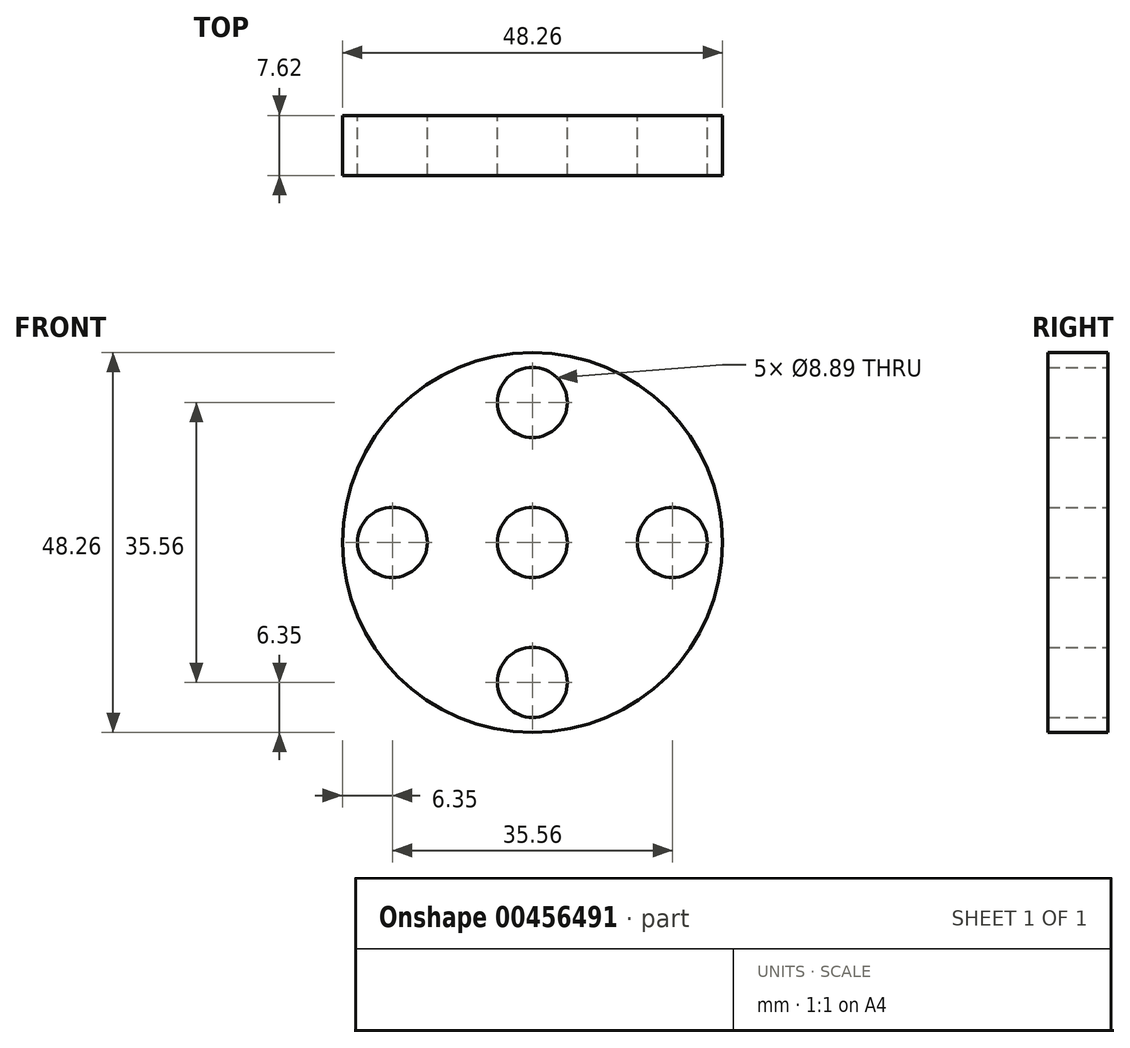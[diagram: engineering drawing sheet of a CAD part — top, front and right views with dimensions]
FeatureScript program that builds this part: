
annotation { "Feature Type Name" : "Feature", "Feature Type Description" : "" }
export const myFeature = defineFeature(function(context is Context, id is Id, definition is map)
    precondition{}
    {
        {
            var Q0;
            Q0=qCreatedBy(makeId("Front.planeOp"),FACE);
            var sketch = newSketch(context, id + "F0", { "sketchPlane" : qUnion([Q0])});
            skCircle(sketch, "E0", {"center": v(0, 0) * mm, "radius": 4.45 * mm});
            skCircle(sketch, "E1", {"center": v(0, 0) * mm, "radius": 6.35 * mm});
            skCircle(sketch, "E2", {"center": v(0, 17.78) * mm, "radius": 4.45 * mm});
            skCircle(sketch, "E3", {"center": v(0, 17.78) * mm, "radius": 6.35 * mm});
            skCircle(sketch, "E4", {"center": v(0, -17.78) * mm, "radius": 4.45 * mm});
            skCircle(sketch, "E5", {"center": v(0, -17.78) * mm, "radius": 6.35 * mm});
            skCircle(sketch, "E6", {"center": v(17.78, 0) * mm, "radius": 4.45 * mm});
            skCircle(sketch, "E7", {"center": v(17.78, 0) * mm, "radius": 6.35 * mm});
            skCircle(sketch, "E8", {"center": v(-17.78, 0) * mm, "radius": 4.45 * mm});
            skCircle(sketch, "E9", {"center": v(-17.78, 0) * mm, "radius": 6.35 * mm});
            skLineSegment(sketch, "E10", {"start": v(-6.35, 17.78) * mm, "end": v(-6.35, 0) * mm});
            skLineSegment(sketch, "E11", {"start": v(6.35, 17.78) * mm, "end": v(6.35, 0) * mm});
            skLineSegment(sketch, "E12", {"start": v(17.78, 6.35) * mm, "end": v(0, 6.35) * mm});
            skLineSegment(sketch, "E13", {"start": v(17.78, -6.35) * mm, "end": v(0, -6.35) * mm});
            skLineSegment(sketch, "E14", {"start": v(-6.35, -17.78) * mm, "end": v(-6.35, 0) * mm});
            skLineSegment(sketch, "E15", {"start": v(6.35, -17.78) * mm, "end": v(6.35, 0) * mm});
            skLineSegment(sketch, "E16", {"start": v(-17.78, 6.35) * mm, "end": v(0, 6.35) * mm});
            skLineSegment(sketch, "E17", {"start": v(-17.78, -6.35) * mm, "end": v(0, -6.35) * mm});
            skCircle(sketch, "E18", {"center": v(0, 0) * mm, "radius": 24.13 * mm});
            skSolve(sketch);
        }
        {
            var Q0;
            Q0=qSketchRegion(id+"F0",true);
            var Q1;
            Q1=makeQuery(id+"F0.imprint","IMPRINT",FACE,{"disambiguationData":[TD([[makeQuery(id+"F0.imprint","IMPRINT",EDGE,{"derivedFrom":sQuery(id+"F0.wireOp",EDGE,"E0")}),-1.0]])]});
            var Q2;
            {var subQ0=sQuery(id+"F0.wireOp",EDGE,"Kdj68EMA-EZRf-t48A-a07Z-1QglQ40iLiN1");Q2=makeQuery(id+"F0.imprint","IMPRINT",FACE,{"disambiguationData":[TD([[makeQuery(id+"F0.imprint","IMPRINT",EDGE,{"derivedFrom":subQ0}),1.0]])]});}
            var Q3;
            {var subQ0=sQuery(id+"F0.wireOp",EDGE,"IB2gJiYN-Zbc6-PHf5-ZDkJ-AlS4u5yRiTVI");Q3=makeQuery(id+"F0.imprint","IMPRINT",FACE,{"disambiguationData":[TD([[makeQuery(id+"F0.imprint","IMPRINT",EDGE,{"derivedFrom":subQ0}),1.0]])]});}
            var Q4;
            {var subQ0=sQuery(id+"F0.wireOp",EDGE,"0Rht0vSG-rdW4-fYld-ASEw-sdk48khHN10M");Q4=makeQuery(id+"F0.imprint","IMPRINT",FACE,{"disambiguationData":[TD([[makeQuery(id+"F0.imprint","IMPRINT",EDGE,{"derivedFrom":subQ0}),-1.0]])]});}
            var Q5;
            {var subQ0=sQuery(id+"F0.wireOp",EDGE,"7g5qWJER-UkHk-XB4v-vlxq-Ywh3V0gzCt1J");Q5=makeQuery(id+"F0.imprint","IMPRINT",FACE,{"disambiguationData":[TD([[makeQuery(id+"F0.imprint","IMPRINT",EDGE,{"derivedFrom":subQ0}),-1.0]])]});}
            var Q6;
            {var subQ0=sQuery(id+"F0.wireOp",EDGE,"yTIMhHz3-IvRj-t1zn-yk0A-B27OQOZ1rXdA");Q6=makeQuery(id+"F0.imprint","IMPRINT",FACE,{"disambiguationData":[TD([[makeQuery(id+"F0.imprint","IMPRINT",EDGE,{"derivedFrom":subQ0}),1.0]])]});}
            var Q7;
            {var subQ0=sQuery(id+"F0.wireOp",EDGE,"zt7eYoZQ-1qTK-d0Ye-JGOG-YsbcoZRo1iPv");Q7=makeQuery(id+"F0.imprint","IMPRINT",FACE,{"disambiguationData":[TD([[makeQuery(id+"F0.imprint","IMPRINT",EDGE,{"derivedFrom":subQ0}),1.0]])]});}
            var Q8;
            {var subQ0=sQuery(id+"F0.wireOp",EDGE,"4NbvyGo8-oQjs-yzer-XTdA-Bz790yNYk6cl");Q8=makeQuery(id+"F0.imprint","IMPRINT",FACE,{"disambiguationData":[TD([[makeQuery(id+"F0.imprint","IMPRINT",EDGE,{"derivedFrom":subQ0}),-1.0]])]});}
            var Q9;
            {var subQ0=sQuery(id+"F0.wireOp",EDGE,"eqKnKHy1-V1mz-GWpX-vf4M-KMWb575NkPCI");Q9=makeQuery(id+"F0.imprint","IMPRINT",FACE,{"disambiguationData":[TD([[makeQuery(id+"F0.imprint","IMPRINT",EDGE,{"derivedFrom":subQ0}),-1.0]])]});}
            var Q10;
            {var subQ0=sQuery(id+"F0.wireOp",EDGE,"4dZgK9fm-a6ys-O8Km-lK4I-ZBlqT9DDIq2p");Q10=makeQuery(id+"F0.imprint","IMPRINT",FACE,{"disambiguationData":[TD([[makeQuery(id+"F0.imprint","IMPRINT",EDGE,{"derivedFrom":subQ0}),1.0]])]});}
            var Q11;
            {var subQ0=sQuery(id+"F0.wireOp",EDGE,"eZOobQb2-sPjm-IE9f-PYXj-G9QqCMmR5pJa");Q11=makeQuery(id+"F0.imprint","IMPRINT",FACE,{"disambiguationData":[TD([[makeQuery(id+"F0.imprint","IMPRINT",EDGE,{"derivedFrom":subQ0}),1.0]])]});}
            var Q12;
            {var subQ0=sQuery(id+"F0.wireOp",EDGE,"Rj4KL7sm-qs8i-fHab-Xu34-aNx6nAbFgW3L");Q12=makeQuery(id+"F0.imprint","IMPRINT",FACE,{"disambiguationData":[TD([[makeQuery(id+"F0.imprint","IMPRINT",EDGE,{"derivedFrom":subQ0}),-1.0]])]});}
            var Q13;
            {var subQ0=sQuery(id+"F0.wireOp",EDGE,"GUNANnpx-HFxo-DPJl-9vIq-FGsHx3uaFTqo");Q13=makeQuery(id+"F0.imprint","IMPRINT",FACE,{"disambiguationData":[TD([[makeQuery(id+"F0.imprint","IMPRINT",EDGE,{"derivedFrom":subQ0}),-1.0]])]});}
            var Q14;
            {var subQ0=sQuery(id+"F0.wireOp",EDGE,"IDcZSpyX-G8bH-AgFG-lNg4-9X1LZLpxGCfa");Q14=makeQuery(id+"F0.imprint","IMPRINT",FACE,{"disambiguationData":[TD([[makeQuery(id+"F0.imprint","IMPRINT",EDGE,{"derivedFrom":subQ0}),-1.0]])]});}
            var Q15;
            {var subQ0=sQuery(id+"F0.wireOp",EDGE,"RcCAguLE-jov0-NsOQ-J9fd-5aWVPCAP70dy");Q15=makeQuery(id+"F0.imprint","IMPRINT",FACE,{"disambiguationData":[TD([[makeQuery(id+"F0.imprint","IMPRINT",EDGE,{"derivedFrom":subQ0}),1.0]])]});}
            var Q16;
            {var subQ0=sQuery(id+"F0.wireOp",EDGE,"3mko06cv-CCnZ-XxRW-BRVZ-f3iim2jyQPBJ");Q16=makeQuery(id+"F0.imprint","IMPRINT",FACE,{"disambiguationData":[TD([[makeQuery(id+"F0.imprint","IMPRINT",EDGE,{"derivedFrom":subQ0}),1.0]])]});}
            var Q17;
            {var subQ0=sQuery(id+"F0.wireOp",EDGE,"ipUqtzeX-P4ue-mGOc-rtnN-ZdVFXNdYJOps");Q17=makeQuery(id+"F0.imprint","IMPRINT",FACE,{"disambiguationData":[TD([[makeQuery(id+"F0.imprint","IMPRINT",EDGE,{"derivedFrom":subQ0}),-1.0]])]});}
            var Q18;
            {var subQ0=sQuery(id+"F0.wireOp",EDGE,"ig39oKl3-C4g6-UK27-omIZ-Wn6p40oPa8TG");Q18=makeQuery(id+"F0.imprint","IMPRINT",FACE,{"disambiguationData":[TD([[makeQuery(id+"F0.imprint","IMPRINT",EDGE,{"derivedFrom":subQ0}),1.0]])]});}
            var Q19;
            {var subQ0=sQuery(id+"F0.wireOp",EDGE,"yZy14Uba-DGiZ-CVV4-Hzny-6y7y5RzOsm5Q");Q19=makeQuery(id+"F0.imprint","IMPRINT",FACE,{"disambiguationData":[TD([[makeQuery(id+"F0.imprint","IMPRINT",EDGE,{"derivedFrom":subQ0}),1.0]])]});}
            var Q20;
            {var subQ0=sQuery(id+"F0.wireOp",EDGE,"VIuSlq0m-v5Ym-oCGE-2FKm-41l9RQB9eqMF");Q20=makeQuery(id+"F0.imprint","IMPRINT",FACE,{"disambiguationData":[TD([[makeQuery(id+"F0.imprint","IMPRINT",EDGE,{"derivedFrom":subQ0}),-1.0]])]});}
            var Q21;
            {var subQ0=sQuery(id+"F0.wireOp",EDGE,"O3mTP4rM-HuvT-6KO2-nrEN-STpfsmbFA0iw");Q21=makeQuery(id+"F0.imprint","IMPRINT",FACE,{"disambiguationData":[TD([[makeQuery(id+"F0.imprint","IMPRINT",EDGE,{"derivedFrom":subQ0}),-1.0]])]});}
            var Q22;
            {var subQ4=sQuery(id+"F0.wireOp",EDGE,"E2");var subQ10=makeQuery(id+"F0.imprint","INTERSECT",VERTEX,{"derivedFrom":[subQ4,sQuery(id+"F0.wireOp",EDGE,"6IOC2M5N-7D7A-1o4P-mhiJ-TW51pYS05NAX")]});Q22=makeQuery(id+"F0.imprint","IMPRINT",FACE,{"disambiguationData":[TD([[makeQuery(id+"F0.imprint","IMPRINT",EDGE,{"disambiguationData":[TD([[subQ10,1.0]])],"derivedFrom":subQ4}),-1.0]])]});}
            var Q23;
            {var subQ0=sQuery(id+"F0.wireOp",EDGE,"E10");var subQ3=sQuery(id+"F0.wireOp",EDGE,"E16");var subQ5=makeQuery(id+"F0.imprint","INTERSECT",VERTEX,{"derivedFrom":[subQ0,subQ3]});Q23=makeQuery(id+"F0.imprint","IMPRINT",FACE,{"disambiguationData":[TD([[makeQuery(id+"F0.imprint","IMPRINT",EDGE,{"disambiguationData":[TD([[subQ5,-1.0]])],"derivedFrom":subQ0}),1.0]])]});}
            var Q24;
            {var subQ0=sQuery(id+"F0.wireOp",EDGE,"E14");var subQ3=sQuery(id+"F0.wireOp",EDGE,"E17");var subQ5=makeQuery(id+"F0.imprint","INTERSECT",VERTEX,{"derivedFrom":[subQ0,subQ3]});Q24=makeQuery(id+"F0.imprint","IMPRINT",FACE,{"disambiguationData":[TD([[makeQuery(id+"F0.imprint","IMPRINT",EDGE,{"disambiguationData":[TD([[subQ5,-1.0]])],"derivedFrom":subQ0}),-1.0]])]});}
            var Q25;
            {var subQ0=sQuery(id+"F0.wireOp",EDGE,"E15");var subQ3=sQuery(id+"F0.wireOp",EDGE,"E13");var subQ5=makeQuery(id+"F0.imprint","INTERSECT",VERTEX,{"derivedFrom":[subQ3,subQ0]});Q25=makeQuery(id+"F0.imprint","IMPRINT",FACE,{"disambiguationData":[TD([[makeQuery(id+"F0.imprint","IMPRINT",EDGE,{"disambiguationData":[TD([[subQ5,-1.0]])],"derivedFrom":subQ3}),-1.0]])]});}
            var Q26;
            {var subQ0=sQuery(id+"F0.wireOp",EDGE,"E11");var subQ3=sQuery(id+"F0.wireOp",EDGE,"E12");var subQ5=makeQuery(id+"F0.imprint","INTERSECT",VERTEX,{"derivedFrom":[subQ0,subQ3]});Q26=makeQuery(id+"F0.imprint","IMPRINT",FACE,{"disambiguationData":[TD([[makeQuery(id+"F0.imprint","IMPRINT",EDGE,{"disambiguationData":[TD([[subQ5,-1.0]])],"derivedFrom":subQ0}),-1.0]])]});}
            var Q27;
            {var subQ4=sQuery(id+"F0.wireOp",EDGE,"E6");var subQ5=makeQuery(id+"F0.imprint","INTERSECT",VERTEX,{"derivedFrom":[subQ4,sQuery(id+"F0.wireOp",EDGE,"eZOobQb2-sPjm-IE9f-PYXj-G9QqCMmR5pJa")]});Q27=makeQuery(id+"F0.imprint","IMPRINT",FACE,{"disambiguationData":[TD([[makeQuery(id+"F0.imprint","IMPRINT",EDGE,{"disambiguationData":[TD([[subQ5,-1.0]])],"derivedFrom":subQ4}),-1.0]])]});}
            var Q28;
            {var subQ4=sQuery(id+"F0.wireOp",EDGE,"E4");var subQ10=makeQuery(id+"F0.imprint","INTERSECT",VERTEX,{"derivedFrom":[subQ4,sQuery(id+"F0.wireOp",EDGE,"jEjaij0X-oPpT-x6fq-c6Pp-KTaQivMJWdQG")]});Q28=makeQuery(id+"F0.imprint","IMPRINT",FACE,{"disambiguationData":[TD([[makeQuery(id+"F0.imprint","IMPRINT",EDGE,{"disambiguationData":[TD([[subQ10,1.0]])],"derivedFrom":subQ4}),-1.0]])]});}
            var Q29;
            {var subQ4=sQuery(id+"F0.wireOp",EDGE,"E8");var subQ5=makeQuery(id+"F0.imprint","INTERSECT",VERTEX,{"derivedFrom":[subQ4,sQuery(id+"F0.wireOp",EDGE,"yZy14Uba-DGiZ-CVV4-Hzny-6y7y5RzOsm5Q")]});Q29=makeQuery(id+"F0.imprint","IMPRINT",FACE,{"disambiguationData":[TD([[makeQuery(id+"F0.imprint","IMPRINT",EDGE,{"disambiguationData":[TD([[subQ5,-1.0]])],"derivedFrom":subQ4}),-1.0]])]});}
            var Q30;
            Q30=makeQuery(id+"F0.imprint","IMPRINT",FACE,{"disambiguationData":[TD([[makeQuery(id+"F0.imprint","IMPRINT",EDGE,{"derivedFrom":sQuery(id+"F0.wireOp",EDGE,"E2")}),-1.0]])]});
            var Q31;
            Q31=makeQuery(id+"F0.imprint","IMPRINT",FACE,{"disambiguationData":[TD([[makeQuery(id+"F0.imprint","IMPRINT",EDGE,{"derivedFrom":sQuery(id+"F0.wireOp",EDGE,"E8")}),-1.0]])]});
            var Q32;
            Q32=makeQuery(id+"F0.imprint","IMPRINT",FACE,{"disambiguationData":[TD([[makeQuery(id+"F0.imprint","IMPRINT",EDGE,{"derivedFrom":sQuery(id+"F0.wireOp",EDGE,"E6")}),-1.0]])]});
            var Q33;
            Q33=makeQuery(id+"F0.imprint","IMPRINT",FACE,{"disambiguationData":[TD([[makeQuery(id+"F0.imprint","IMPRINT",EDGE,{"derivedFrom":sQuery(id+"F0.wireOp",EDGE,"E4")}),-1.0]])]});
            var Q34;
            {var subQ0=sQuery(id+"F0.wireOp",EDGE,"E16");var subQ1=sQuery(id+"F0.wireOp",EDGE,"E9");var subQ2=makeQuery(id+"F0.imprint","INTERSECT",VERTEX,{"derivedFrom":[subQ1,subQ0]});Q34=makeQuery(id+"F0.imprint","IMPRINT",FACE,{"disambiguationData":[TD([[makeQuery(id+"F0.imprint","IMPRINT",EDGE,{"disambiguationData":[TD([[subQ2,1.0]])],"derivedFrom":subQ1}),-1.0]])]});}
            var Q35;
            {var subQ1=sQuery(id+"F0.wireOp",EDGE,"E5");var subQ5=sQuery(id+"F0.wireOp",EDGE,"E14");var subQ6=makeQuery(id+"F0.imprint","INTERSECT",VERTEX,{"derivedFrom":[subQ1,subQ5]});Q35=makeQuery(id+"F0.imprint","IMPRINT",FACE,{"disambiguationData":[TD([[makeQuery(id+"F0.imprint","IMPRINT",EDGE,{"disambiguationData":[TD([[subQ6,1.0]])],"derivedFrom":subQ1}),-1.0]])]});}
            var Q36;
            {var subQ1=sQuery(id+"F0.wireOp",EDGE,"E7");var subQ7=sQuery(id+"F0.wireOp",EDGE,"E12");var subQ9=makeQuery(id+"F0.imprint","INTERSECT",VERTEX,{"derivedFrom":[subQ1,subQ7]});Q36=makeQuery(id+"F0.imprint","IMPRINT",FACE,{"disambiguationData":[TD([[makeQuery(id+"F0.imprint","IMPRINT",EDGE,{"disambiguationData":[TD([[subQ9,-1.0]])],"derivedFrom":subQ1}),-1.0]])]});}
            var Q37;
            {var subQ5=sQuery(id+"F0.wireOp",EDGE,"E10");var subQ6=sQuery(id+"F0.wireOp",EDGE,"E3");var subQ7=makeQuery(id+"F0.imprint","INTERSECT",VERTEX,{"derivedFrom":[subQ6,subQ5]});Q37=makeQuery(id+"F0.imprint","IMPRINT",FACE,{"disambiguationData":[TD([[makeQuery(id+"F0.imprint","IMPRINT",EDGE,{"disambiguationData":[TD([[subQ7,-1.0]])],"derivedFrom":subQ6}),-1.0]])]});}
            extrude(context, id + "F1", {"entities" : qUnion([Q0, Q1, Q2, Q3, Q4, Q5, Q6, Q7, Q8, Q9, Q10, Q11, Q12, Q13, Q14, Q15, Q16, Q17, Q18, Q19, Q20, Q21, Q22, Q23, Q24, Q25, Q26, Q27, Q28, Q29, Q30, Q31, Q32, Q33, Q34, Q35, Q36, Q37]), "depth" : 7.62 * mm, "offsetDistance" : 25.4 * mm});
        }
    });
